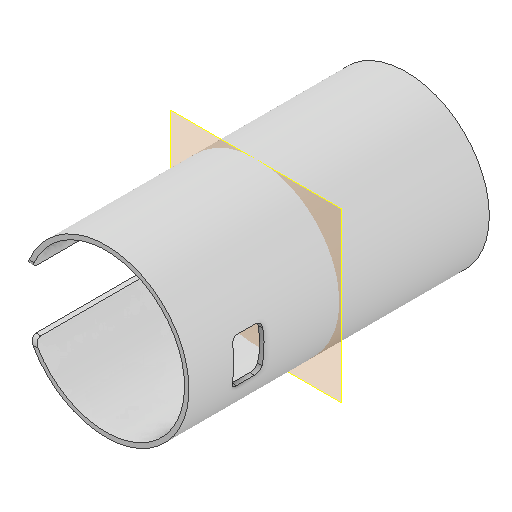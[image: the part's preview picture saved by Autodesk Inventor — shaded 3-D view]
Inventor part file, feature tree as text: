
AUTODESK INVENTOR PART (.ipt)
format: ipt  version: 2022 (Build 260153000, 153)  size: 186,880 bytes
history: native  units: mm
features: other x4, extrude x3, sketch x3, plane x1, fillet x1, projected_geometry x1, reference x1
ambient origin geometry x8: Origin, YZ Plane, XZ Plane, XY Plane, X Axis, Y Axis, Z Axis, Center Point
bodies: Volumenkörper1 (feature_tree)
feature tree (14):
  plane  "Arbeitsebene1"
  extrude  "Extrusion1"  Depth=52.4mm
  extrude  "Extrusion3"  Depth=20.0mm
  fillet  "Rundung1"  Radius=55.0mm
  extrude  "Extrusion4"  Depth=2.0mm
  sketch  "Skizze1"  dims[d0=100.0mm d1=0.0mm d11=52.4mm]
  sketch  "Skizze3"  dims[d12=55.4mm d13=20.0mm d14=55.0mm]
  sketch  "Skizze4"  dims[d15=75.0mm d16=0.0mm d17=2.0mm d18=15.0mm d19=10.0mm d20=15.0mm d21=2.0mm d22=0.0mm d23=0.0mm]
  projected_geometry  "Projizierte Kontur3"
  reference  "Referenz3"
  other  "Planktoscope_Mini_v0.iam"
  other  "Matchboxscope_middle2_v2:1"
  other  "Planktoscope_Mini_Peristalticpump:1"
  other  "Pump_Base_Motor:1"
